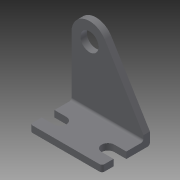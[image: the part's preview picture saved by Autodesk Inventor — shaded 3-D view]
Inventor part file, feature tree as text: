
AUTODESK INVENTOR PART (.ipt)
format: ipt  version: 2014 (Build 180170000, 170)  size: 188,416 bytes
history: native  units: in
note: dims shown in document units (in); Inventor stores cm internally (conversion verified against a paired STEP export)
features: other x147, sketch x8, extrude x5, hole x3
ambient origin geometry x8: Origin, YZ Plane, XZ Plane, XY Plane, X Axis, Y Axis, Z Axis, Center Point
bodies: Solid1 (feature_tree)
feature tree (163):
  extrude  "Extrusion1"  Depth=1.0in TaperAngle=0.0deg
  extrude  "Extrusion2"  Depth=0.1345in TaperAngle=0.0deg
  hole  "Hole1"  [1 undecoded]
  hole  "Hole2"  [1 undecoded]
  hole  "Hole3"  [1 undecoded]
  sketch  "Sketch_6"
  sketch  "Sketch_7"
  extrude  "Extrusion3"  [1 undecoded]
  extrude  "Extrusion4"  [1 undecoded]
  extrude  "Extrusion5"  [1 undecoded]
  other  "a1_XY"
  other  "a1_YZ"
  other  "a1_ZX"
  other  "a1_X"
  other  "a1_Y"
  other  "a1_Z"
  other  "a1_Center"
  other  "a2_XY"
  other  "a2_YZ"
  other  "a2_ZX"
  other  "a2_X"
  other  "a2_Y"
  other  "a2_Z"
  other  "a2_Center"
  other  "b1_XY"
  other  "b1_YZ"
  other  "b1_ZX"
  other  "b1_X"
  other  "b1_Y"
  other  "b1_Z"
  other  "b1_Center"
  other  "b2_XY"
  other  "b2_YZ"
  other  "b2_ZX"
  other  "b2_X"
  other  "b2_Y"
  other  "b2_Z"
  other  "b2_Center"
  other  "d1_XY"
  other  "d1_YZ"
  other  "d1_ZX"
  other  "d1_X"
  other  "d1_Y"
  other  "d1_Z"
  other  "d1_Center"
  other  "d2_XY"
  other  "d2_YZ"
  other  "d2_ZX"
  other  "d2_X"
  other  "d2_Y"
  other  "d2_Z"
  other  "d2_Center"
  other  "e1_XY"
  other  "e1_YZ"
  other  "e1_ZX"
  other  "e1_X"
  other  "e1_Y"
  other  "e1_Z"
  other  "e1_Center"
  other  "e2_XY"
  other  "e2_YZ"
  other  "e2_ZX"
  other  "e2_X"
  other  "e2_Y"
  other  "e2_Z"
  other  "e2_Center"
  other  "f1_XY"
  other  "f1_YZ"
  other  "f1_ZX"
  other  "f1_X"
  other  "f1_Y"
  other  "f1_Z"
  other  "f1_Center"
  other  "f2_XY"
  other  "f2_YZ"
  other  "f2_ZX"
  other  "f2_X"
  other  "f2_Y"
  other  "f2_Z"
  other  "f2_Center"
  other  "g1_XY"
  other  "g1_YZ"
  other  "g1_ZX"
  other  "g1_X"
  other  "g1_Y"
  other  "g1_Z"
  other  "g1_Center"
  other  "g2_XY"
  other  "g2_YZ"
  other  "g2_ZX"
  other  "g2_X"
  other  "g2_Y"
  other  "g2_Z"
  other  "g2_Center"
  other  "h1_XY"
  other  "h1_YZ"
  other  "h1_ZX"
  other  "h1_X"
  other  "h1_Y"
  other  "h1_Z"
  other  "h1_Center"
  other  "h2_XY"
  other  "h2_YZ"
  other  "h2_ZX"
  other  "h2_X"
  other  "h2_Y"
  other  "h2_Z"
  other  "h2_Center"
  other  "i_XY"
  other  "i_YZ"
  other  "i_ZX"
  other  "i_X"
  other  "i_Y"
  other  "i_Z"
  other  "i_Center"
  other  "j1_XY"
  other  "j1_YZ"
  other  "j1_ZX"
  other  "j1_X"
  other  "j1_Y"
  other  "j1_Z"
  other  "j1_Center"
  other  "j2_XY"
  other  "j2_YZ"
  other  "j2_ZX"
  other  "j2_X"
  other  "j2_Y"
  other  "j2_Z"
  other  "j2_Center"
  other  "k11_XY"
  other  "k11_YZ"
  other  "k11_ZX"
  other  "k11_X"
  other  "k11_Y"
  other  "k11_Z"
  other  "k11_Center"
  other  "k12_XY"
  other  "k12_YZ"
  other  "k12_ZX"
  other  "k12_X"
  other  "k12_Y"
  other  "k12_Z"
  other  "k12_Center"
  other  "to_dummy_L_XY"
  other  "to_dummy_L_YZ"
  other  "to_dummy_L_ZX"
  other  "to_dummy_L_X"
  other  "to_dummy_L_Y"
  other  "to_dummy_L_Z"
  other  "to_dummy_L_Center"
  other  "to_pin_L_XY"
  other  "to_pin_L_YZ"
  other  "to_pin_L_ZX"
  other  "to_pin_L_X"
  other  "to_pin_L_Y"
  other  "to_pin_L_Z"
  other  "to_pin_L_Center"
  sketch  "Sketch_1"  dims[d0=1.5in d1=0.0in d2=1.0in d3=0.0in]
  sketch  "Sketch_2"  dims[d4=0.3775in d5=0.75in d6=0.375in d7=0.25in d8=0.5635in d9=0.1345in d10=0.0in]
  sketch  "Sketch3"  dims[d11=0.266in d12=0.75in d13=0.375in d14=0.25in d15=0.5635in d16=0.1345in d17=0.0in]
  sketch  "Sketch4"  dims[d18=0.266in d19=0.75in d20=0.375in d21=0.25in d22=0.5635in d23=0.1345in d24=0.0in d25=0.1345in d26=0.0in]
  sketch  "Sketch5"  dims[d27=0.1345in d28=0.0in d29=0.1345in d30=0.0in]
  sketch  "Sketch_8"
note: 6 required parameter values undecoded (feature->parameter linkage not recoverable at this tier; creation-order binding heuristic only, values carry confidence <= 0.55)
